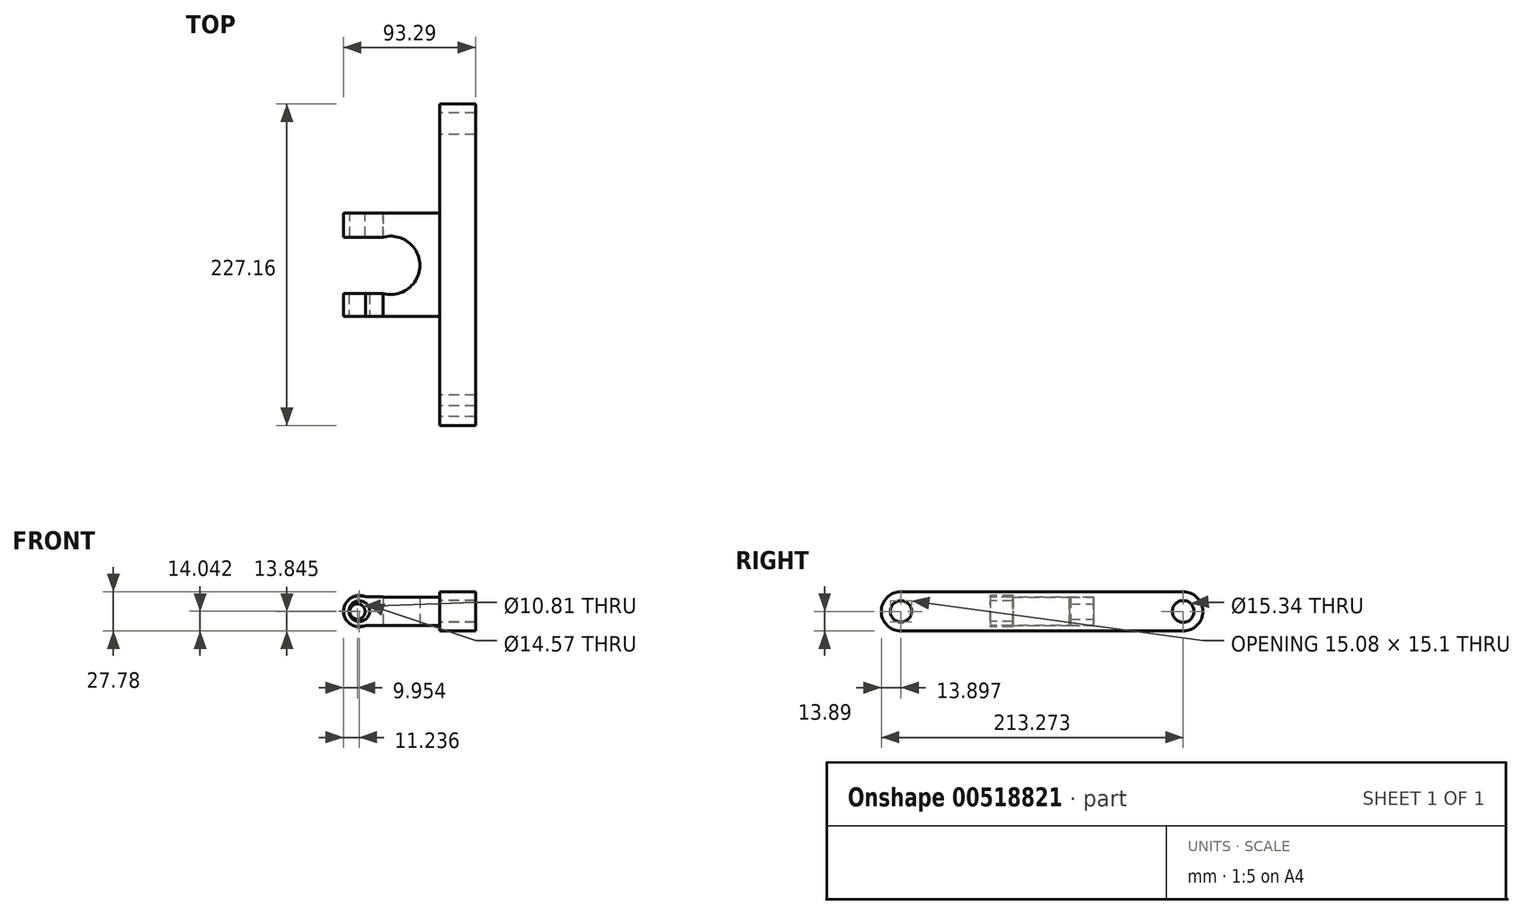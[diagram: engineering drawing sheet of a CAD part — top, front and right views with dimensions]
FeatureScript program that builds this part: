
annotation { "Feature Type Name" : "Feature", "Feature Type Description" : "" }
export const myFeature = defineFeature(function(context is Context, id is Id, definition is map)
    precondition{}
    {
        {
            var Q0;
            Q0=qCreatedBy(makeId("Right.planeOp"),FACE);
            var sketch = newSketch(context, id + "F0", { "sketchPlane" : qUnion([Q0])});
            skArc(sketch, "E0", {"start": v(-99.7, 13.89) * mm, "mid": v(-113.58, 0) * mm, "end": v(-99.7, -13.89) * mm});
            skLineSegment(sketch, "E1.bottom", {"start": v(-99.7, 13.89) * mm, "end": v(99.7, 13.89) * mm});
            skLineSegment(sketch, "E1.top", {"start": v(-99.7, -13.89) * mm, "end": v(99.7, -13.89) * mm});
            skLineSegment(sketch, "E1.left", {"start": v(-99.7, 13.89) * mm, "end": v(-99.7, -13.89) * mm});
            skLineSegment(sketch, "E1.right", {"start": v(99.7, 13.89) * mm, "end": v(99.7, -13.89) * mm});
            skPoint(sketch, "E1.middle", {"position": v(0, 0) * mm});
            skPoint(sketch, "E2.center.orphan", {"position": v(78.93, 0) * mm});
            skPoint(sketch, "E3.center.orphan", {"position": v(76.32, 0) * mm});
            skArc(sketch, "E4", {"start": v(99.7, -13.89) * mm, "mid": v(113.58, 0) * mm, "end": v(99.7, 13.89) * mm});
            skArc(sketch, "E5.0", {"start": v(-99.72, 7.54) * mm, "mid": v(-107.23, 0) * mm, "end": v(-99.72, -7.54) * mm});
            skArc(sketch, "E6", {"start": v(-92.14, 0) * mm, "mid": v(-94.35, 5.34) * mm, "end": v(-99.7, 7.55) * mm});
            skArc(sketch, "E7", {"start": v(-92.14, 0) * mm, "mid": v(-94.36, -5.34) * mm, "end": v(-99.72, -7.54) * mm});
            skArc(sketch, "E8", {"start": v(-106.96, 2) * mm, "mid": v(-105.69, -4.58) * mm, "end": v(-99.7, -7.55) * mm});
            skArc(sketch, "E9", {"start": v(-99.7, 7.55) * mm, "mid": v(-104.27, 6) * mm, "end": v(-106.96, 2) * mm});
            skArc(sketch, "E10.0", {"start": v(-99.7, 7.54) * mm, "mid": v(-107.23, 0) * mm, "end": v(-99.7, -7.54) * mm});
            skArc(sketch, "E11", {"start": v(92.53, 2.74) * mm, "mid": v(107.24, -1.4) * mm, "end": v(92.02, 0) * mm});
            skArc(sketch, "E12", {"start": v(92.53, 2.74) * mm, "mid": v(92.15, 1.4) * mm, "end": v(92.02, 0) * mm});
            skSolve(sketch);
        }
        {
            var Q0;
            {var subQ1=sQuery(id+"F0.wireOp",EDGE,"E0");Q0=makeQuery(id+"F0.imprint","IMPRINT",FACE,{"disambiguationData":[TD([[makeQuery(id+"F0.imprint","IMPRINT",EDGE,{"derivedFrom":subQ1}),1.0]])]});}
            var Q1;
            {var subQ6=sQuery(id+"F0.wireOp",EDGE,"E1.bottom");Q1=makeQuery(id+"F0.imprint","IMPRINT",FACE,{"disambiguationData":[TD([[makeQuery(id+"F0.imprint","IMPRINT",EDGE,{"derivedFrom":subQ6}),-1.0]])]});}
            var Q2;
            {var subQ0=sQuery(id+"F0.wireOp",EDGE,"E4");Q2=makeQuery(id+"F0.imprint","IMPRINT",FACE,{"disambiguationData":[TD([[makeQuery(id+"F0.imprint","IMPRINT",EDGE,{"derivedFrom":subQ0}),1.0]])]});}
            extrude(context, id + "F1", {"entities" : qUnion([Q0, Q1, Q2]), "depth" : 25.4 * mm, "offsetDistance" : 25.4 * mm});
        }
        {
            var Q0;
            Q0=qCreatedBy(makeId("Top.planeOp"),FACE);
            var sketch = newSketch(context, id + "F2", { "sketchPlane" : qUnion([Q0])});
            skLineSegment(sketch, "E13", {"start": v(0, 36.43) * mm, "end": v(0, 0) * mm});
            skLineSegment(sketch, "E14", {"start": v(0, 0) * mm, "end": v(0, -36.43) * mm});
            skLineSegment(sketch, "E15.bottom", {"start": v(0, 36.43) * mm, "end": v(-39.98, 36.43) * mm});
            skLineSegment(sketch, "E15.top", {"start": v(0, -36.47) * mm, "end": v(-39.98, -36.47) * mm});
            skLineSegment(sketch, "E15.left", {"start": v(0, 36.43) * mm, "end": v(0, -36.47) * mm});
            skLineSegment(sketch, "E15.right", {"start": v(-39.98, 36.43) * mm, "end": v(-39.98, 19.48) * mm});
            skArc(sketch, "E16", {"start": v(-39.98, -20.3) * mm, "mid": v(-13.9, -0.41) * mm, "end": v(-39.98, 19.48) * mm});
            skLineSegment(sketch, "E17.trimOffspring", {"start": v(-39.98, -20.3) * mm, "end": v(-39.98, -36.47) * mm});
            skSolve(sketch);
        }
        {
            var Q0;
            {var subQ1=sQuery(id+"F2.wireOp",EDGE,"E15.bottom");Q0=makeQuery(id+"F2.imprint","IMPRINT",FACE,{"disambiguationData":[TD([[makeQuery(id+"F2.imprint","IMPRINT",EDGE,{"derivedFrom":subQ1}),1.0]])]});}
            extrude(context, id + "F3", {"entities" : qUnion([Q0]), "operationType" : NewBodyOperationType.ADD, "endBound" : BoundingType.SYMMETRIC, "depth" : 19.8 * mm, "offsetDistance" : 25.4 * mm});
        }
        {
            var Q0;
            Q0=makeQuery(id+"F3.opExtrude","SWEPT_FACE",FACE,{"disambiguationData":[OSD([sQuery(id+"F2.wireOp",EDGE,"E15.bottom")])]});
            var sketch = newSketch(context, id + "F4", { "sketchPlane" : qUnion([Q0])});
            skLineSegment(sketch, "E18.bottom", {"start": v(39.98, 9.9) * mm, "end": v(57.94, 9.9) * mm});
            skLineSegment(sketch, "E18.top", {"start": v(39.98, -10) * mm, "end": v(57.94, -10) * mm});
            skLineSegment(sketch, "E18.left", {"start": v(39.98, 9.9) * mm, "end": v(39.98, -10) * mm});
            skArc(sketch, "E19", {"start": v(57.94, -10) * mm, "mid": v(67.89, -0.05) * mm, "end": v(57.94, 9.9) * mm});
            skCircle(sketch, "E20", {"center": v(57.94, -0.05) * mm, "radius": 5.4 * mm});
            skSolve(sketch);
        }
        {
            var Q0;
            {var subQ4=sQuery(id+"F4.wireOp",EDGE,"E18.bottom");Q0=makeQuery(id+"F4.imprint","IMPRINT",FACE,{"disambiguationData":[TD([[makeQuery(id+"F4.imprint","IMPRINT",EDGE,{"derivedFrom":subQ4}),-1.0]])]});}
            extrude(context, id + "F5", {"entities" : qUnion([Q0]), "operationType" : NewBodyOperationType.ADD, "oppositeDirection" : true, "depth" : 17.02 * mm, "offsetDistance" : 25.4 * mm});
        }
        {
            var Q0;
            Q0=makeQuery(id+"F3.opExtrude","SWEPT_FACE",FACE,{"disambiguationData":[OSD([sQuery(id+"F2.wireOp",EDGE,"E15.top")])]});
            var sketch = newSketch(context, id + "F6", { "sketchPlane" : qUnion([Q0])});
            skLineSegment(sketch, "E21.bottom", {"start": v(-39.98, -9.9) * mm, "end": v(-52.1, -9.9) * mm});
            skLineSegment(sketch, "E21.top", {"start": v(-39.98, 10.2) * mm, "end": v(-52.1, 10.2) * mm});
            skLineSegment(sketch, "E21.left", {"start": v(-39.98, -9.9) * mm, "end": v(-39.98, 10.2) * mm});
            skLineSegment(sketch, "E21.right", {"start": v(-52.1, -9.9) * mm, "end": v(-52.1, 10.2) * mm});
            skArc(sketch, "E22", {"start": v(-52.1, 10.2) * mm, "mid": v(-67.7, 0.15) * mm, "end": v(-52.1, -9.9) * mm});
            skCircle(sketch, "E23", {"center": v(-56.65, 0.15) * mm, "radius": 7.29 * mm});
            skSolve(sketch);
        }
        {
            var Q0;
            {var subQ4=sQuery(id+"F6.wireOp",EDGE,"E21.bottom");Q0=makeQuery(id+"F6.imprint","IMPRINT",FACE,{"disambiguationData":[TD([[makeQuery(id+"F6.imprint","IMPRINT",EDGE,{"derivedFrom":subQ4}),-1.0]])]});}
            var Q1;
            {var subQ0=sQuery(id+"F6.wireOp",EDGE,"E22");Q1=makeQuery(id+"F6.imprint","IMPRINT",FACE,{"disambiguationData":[TD([[makeQuery(id+"F6.imprint","IMPRINT",EDGE,{"derivedFrom":subQ0}),1.0]])]});}
            extrude(context, id + "F7", {"entities" : qUnion([Q0, Q1]), "operationType" : NewBodyOperationType.ADD, "oppositeDirection" : true, "depth" : 16 * mm, "offsetDistance" : 25.4 * mm});
        }
    });
